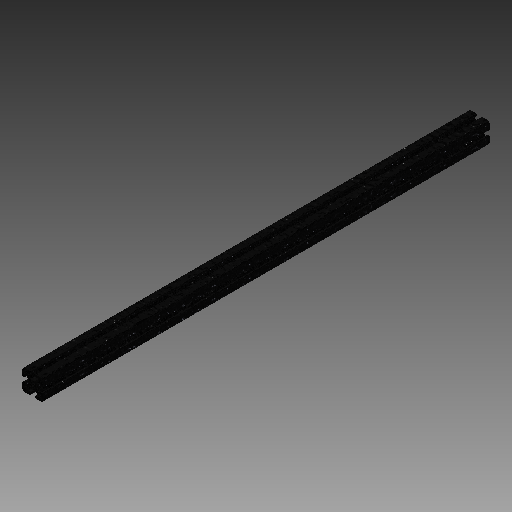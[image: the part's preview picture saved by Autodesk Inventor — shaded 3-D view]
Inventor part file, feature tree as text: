
AUTODESK INVENTOR PART (.ipt)
format: ipt  version: 2019 (Build 230136000, 136)  size: 249,344 bytes
history: native  units: in
note: dims shown in document units (in); Inventor stores cm internally (conversion verified against a paired STEP export)
features: plane x1, extrude x1, sketch x1
ambient origin geometry x8: Origin, YZ Plane, XZ Plane, XY Plane, X Axis, Y Axis, Z Axis, Center Point
bodies: Solid1 (feature_tree)
feature tree (3):
  plane  "Work Plane1"
  extrude  "Extrusion1"  [1 undecoded]
  sketch  "Sketch1"  dims[d0=32.5in d1=0.0in]
note: 1 required parameter value undecoded (feature->parameter linkage not recoverable at this tier; creation-order binding heuristic only, values carry confidence <= 0.55)
